# Revit family: SNS Merlin 3000S Interlock
name_source: partatom
category: Electrical Equipment
units: mm (PartAtom-declared; Revit-internal decimal feet)

## family parameters
Always vertical = Yes
Cut with Voids When Loaded = No
OmniClass Number = 23.80.30.11.17
OmniClass Title = Distribution Boards and Control Panels
Part Type = Other Panel
Room Calculation Point = No
Round Connector Dimension = Use Diameter
Shared = No
Work Plane-Based = No

## types (1)
- SNS Merlin 3000S
    Default Height = 4' - 0"
    Description = The Merlin 3000S is an energy saving system designed specifically for commercial kitchens. The system acts an interlock between the ventilation and the gas solenoid valve, while also varying the speed of the ventilation via a 0-10vdc output.
    Load = 120 VA
    Manufacturer = S&S Northern Ltd.
    Model = SNS Merlin 3000S
    Product Information = https://snsnorthern.com
    Type Comments = The Merlin 3000S is an energy saving system designed specifically for commercial kitchens. The system acts an interlock between the ventilation and the gas solenoid valve, while also varying the speed of the ventilation via a 0-10vdc output.
    URL = https://snsnorthern.com
    Voltage = 120VAC

## geometry (parser evidence)
native form markers: Sweep x12
no freeform markers — native parametric forms only
